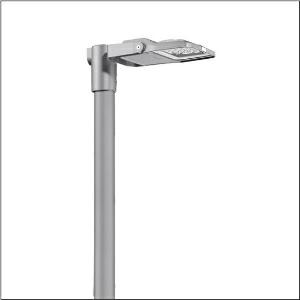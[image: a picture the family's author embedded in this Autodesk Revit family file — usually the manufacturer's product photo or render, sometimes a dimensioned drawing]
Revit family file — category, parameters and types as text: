
# Revit family: floodlight_fl_21_iq_micro___pl52_5xa7761a4d3a_5d98
name_source: partatom
category: Lighting Fixtures
units: mm (PartAtom-declared; Revit-internal decimal feet)

## family parameters
Cut with Voids When Loaded = No
Host = Face
Light Source = No
Part Type = Normal
Room Calculation Point = No
Round Connector Dimension = Use Diameter
Shared = No

## types (1)
- --- (1 x LED, 3010 lm, 23.1 W, 4000K)
    Apparent Load = 23 VA
    CIE Flux Codes = 26 60 98 100 100
    Color Rendering = 70
    Color Temperature = 4000K
    Default Elevation = 1800 mm
    Description = Floodlight FL 21 iQ micro, floodlight, primary light control with lens, of PMMA, primary optical cover: protective disc, of toughened safety glass, transparent, light distribution: PL52, light emission: direct distribution, installation type: surface-mounted, LED, High Power LED, rated luminous flux: 3.010lm, luminous efficacy: 130lm/W, light colour: 740, colour temperature: 4000K, control: optimised constant luminous flux control (CLO 2.0), Desk-Remote (wireless, voltage-free reading and setting of iQ features in the workshop via application-optimized NFC function/RFID function), Light-Fading, Smart-Wire, Night-Set, Lumen-Switch, Temp-Guard, Auto-Match, with terminal, 6-pole, mains connection: 220..240V, AC, 50/60Hz, start of lifetime: 23W, end of service life: 24W, reduction: 11W, luminaire housing, of diecast aluminium, powder-coated, Siteco® metallic grey (DB 702S), corrosivity category C5 mid according to DIN EN ISO 12944, sealing non-destructively replaceable, please order mast flange separately, mast bracket, of steel, galvanised, powder-coated, Siteco® metallic grey (DB 702S), protection rating (complete): IP66, insulation class (complete): insulation class II (safety insulation), certification: CE, ENEC, VDE, protection symbol: D, impact resistance: IK07, permissible operating ambient temperature: -40..+40°C, permissible operating ambient temperature for outdoor applications: -40..+50°C, standard: DIN EN 12944, LABS conformity tested according to VDMA 24364:2018-05, packaging unit: 1 piece

Light Distribution: PL52
    Height = 65 mm
    Lamp = 1 x LED
    Lamp Light Flux = 3010 lm
    Lamp Power = 23.1 W
    Lamp count = 1
    Length = 312 mm
    Luminous efficacy = 130 lm/W
    Manufacturer = Siteco
    ModVariant = No
    Model = 5XA7761A4D3A
    Number of Poles = 1
    OnlyDefault = Yes
    Power Factor = 1
    Product Name = Floodlight FL 21 iQ micro | PL52
    Product group = floodlight | pylon annexe
    ProductGroupID = 6200
    Protection Class = Protection class II
    Protection Degree = IP 66
    RLX_Detail_Level = 1
    RLX_Emergency_Light_Flux = 0 lm
    RLX_Emergency_Type = 0
    RLX_Emergency_Type_DB = No
    RlxData = <blob elided: 101937 chars, md5=246e7644>
    Socket = socket
    Standby Power = 0 W
    System Light Flux = 3010 lm
    System Power = 23 W
    Type Comments = factory setting: luminous flux: 100 % | dim-lin: 254 | 455 mA
    Type Image = l_1007121.jpg
    URL = http://relux.com
    VarID = @adj_110777
    Voltage = 0 V
    Weight = 0.00 kg
    Width = 230 mm

## geometry (parser evidence)
native form markers: Blend x4, Sweep x12
no freeform markers — native parametric forms only
